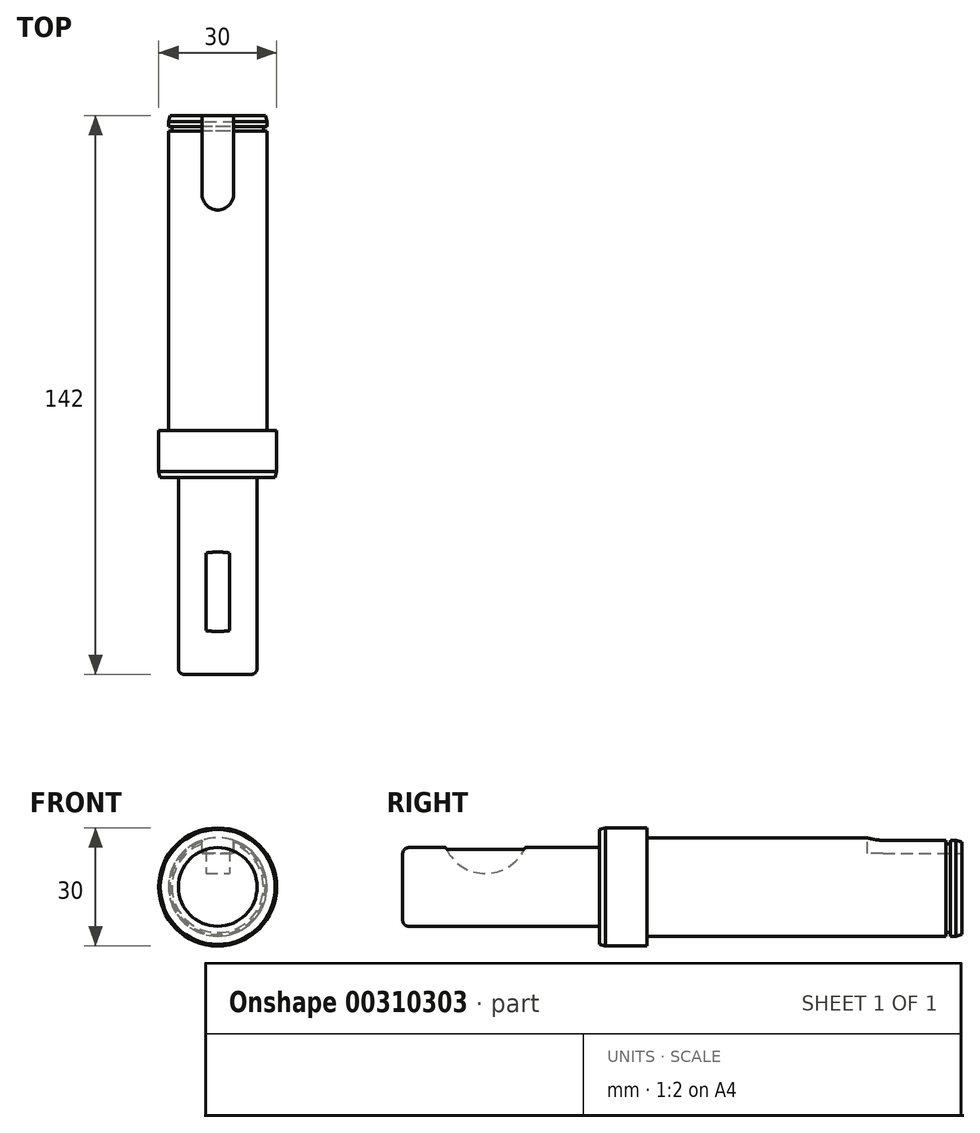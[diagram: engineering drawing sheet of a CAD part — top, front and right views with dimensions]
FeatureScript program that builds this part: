
annotation { "Feature Type Name" : "Feature", "Feature Type Description" : "" }
export const myFeature = defineFeature(function(context is Context, id is Id, definition is map)
    precondition{}
    {
        {
            var Q0;
            Q0=qCreatedBy(makeId("Front.planeOp"),FACE);
            var sketch = newSketch(context, id + "F0", { "sketchPlane" : qUnion([Q0])});
            skCircle(sketch, "E0", {"center": v(0, 0) * mm, "radius": 12.5 * mm});
            skSolve(sketch);
        }
        {
            var Q0;
            Q0=makeQuery(id+"F0.imprint","IMPRINT",FACE,{"disambiguationData":[TD([[makeQuery(id+"F0.imprint","IMPRINT",EDGE,{"derivedFrom":sQuery(id+"F0.wireOp",EDGE,"E0")}),1.0]])]});
            extrude(context, id + "F1", {"entities" : qUnion([Q0]), "depth" : 80 * mm});
        }
        {
            var Q0;
            Q0=makeQuery(id+"F1.opExtrude","CAP_FACE",FACE,{"disambiguationData":[OSD([sQuery(id+"F0.wireOp",EDGE,"E0")])],"isStart":false});
            var sketch = newSketch(context, id + "F2", { "sketchPlane" : qUnion([Q0])});
            skCircle(sketch, "E1", {"center": v(0, 0) * mm, "radius": 15 * mm});
            skSolve(sketch);
        }
        {
            var Q0;
            Q0 = qSketchRegion(id + "F2", true);
            var Q1;
            Q1=sQuery(id+"F2.wireOp",EDGE,"E1");
            extrude(context, id + "F3", {"entities" : qUnion([Q0]), "operationType" : NewBodyOperationType.ADD, "surfaceEntities" : qUnion([Q1]), "depth" : 12 * mm});
        }
        {
            var Q0;
            Q0=makeQuery(id+"F3.opExtrude","CAP_FACE",FACE,{"disambiguationData":[OSD([sQuery(id+"F2.wireOp",EDGE,"E1")])],"isStart":false});
            var sketch = newSketch(context, id + "F4", { "sketchPlane" : qUnion([Q0])});
            skCircle(sketch, "E2", {"center": v(0, 0) * mm, "radius": 10 * mm});
            skSolve(sketch);
        }
        {
            var Q0;
            Q0=makeQuery(id+"F4.imprint","IMPRINT",FACE,{"disambiguationData":[TD([[makeQuery(id+"F4.imprint","IMPRINT",EDGE,{"derivedFrom":sQuery(id+"F4.wireOp",EDGE,"E2")}),1.0]])]});
            extrude(context, id + "F5", {"entities" : qUnion([Q0]), "operationType" : NewBodyOperationType.ADD, "depth" : 50 * mm});
        }
        {
            var Q0;
            Q0=makeQuery(id+"F1.opExtrude","CAP_EDGE",EDGE,{"disambiguationData":[OSD([sQuery(id+"F0.wireOp",EDGE,"E0")])],"isStart":true});
            chamfer(context, id + "F6", {"entities" : qUnion([Q0]), "chamferType" : ChamferType.OFFSET_ANGLE, "width" : 0.4 * mm, "oppositeDirection" : true, "angle" : 75 * degree, "tangentPropagation" : true});
        }
        {
            var Q0;
            Q0=makeQuery(id+"F3.opExtrude","CAP_EDGE",EDGE,{"disambiguationData":[OSD([sQuery(id+"F2.wireOp",EDGE,"E1")])],"isStart":false});
            chamfer(context, id + "F7", {"entities" : qUnion([Q0]), "chamferType" : ChamferType.OFFSET_ANGLE, "width" : 0.4 * mm, "oppositeDirection" : false, "angle" : 75 * degree, "tangentPropagation" : true});
        }
        {
            var Q0;
            Q0=makeQuery(id+"F5.opExtrude","CAP_EDGE",EDGE,{"disambiguationData":[OSD([sQuery(id+"F4.wireOp",EDGE,"E2")])],"isStart":false});
            fillet(context, id + "F8", {"entities" : qUnion([Q0]), "radius" : 1.5 * mm, "tangentPropagation" : true, "allowEdgeOverflow" : false});
        }
        {
            var Q0;
            Q0=qCreatedBy(makeId("Top.planeOp"),FACE);
            cPlane(context, id + "F9", {"entities" : qUnion([Q0]), "cplaneType" : CPlaneType.OFFSET, "offset" : 12.5 * mm, "width" : 150 * mm, "height" : 150 * mm});
        }
        {
            var Q0;
            Q0=qCreatedBy(id+"F9.planeOp",FACE);
            var sketch = newSketch(context, id + "F10", { "sketchPlane" : qUnion([Q0])});
            skLineSegment(sketch, "E3", {"start": v(-4, -20) * mm, "end": v(-4, 31.78) * mm});
            skLineSegment(sketch, "E4", {"start": v(-4, 31.78) * mm, "end": v(4, 31.78) * mm});
            skLineSegment(sketch, "E5", {"start": v(4, 31.78) * mm, "end": v(4, -20) * mm});
            skArc(sketch, "E6", {"start": v(-4, -20) * mm, "mid": v(0, -24) * mm, "end": v(4, -20) * mm});
            skSolve(sketch);
        }
        {
            var Q0;
            Q0=makeQuery(id+"F10.imprint","IMPRINT",FACE,{"disambiguationData":[TD([[makeQuery(id+"F10.imprint","IMPRINT",EDGE,{"derivedFrom":sQuery(id+"F10.wireOp",EDGE,"E3")}),-1.0]])]});
            extrude(context, id + "F11", {"entities" : qUnion([Q0]), "operationType" : NewBodyOperationType.REMOVE, "oppositeDirection" : true, "depth" : 4 * mm});
        }
        {
            var Q0;
            Q0=qCreatedBy(makeId("Right.planeOp"),FACE);
            var sketch = newSketch(context, id + "F12", { "sketchPlane" : qUnion([Q0])});
            skLineSegment(sketch, "E7", {"start": v(-2.8, -11.6) * mm, "end": v(-2.8, -12.5) * mm});
            skLineSegment(sketch, "E8", {"start": v(-2.8, -12.5) * mm, "end": v(-4, -12.5) * mm});
            skLineSegment(sketch, "E9", {"start": v(-4, -12.5) * mm, "end": v(-4, -11.6) * mm});
            skLineSegment(sketch, "E10", {"start": v(-4, -11.6) * mm, "end": v(-2.8, -11.6) * mm});
            skSolve(sketch);
        }
        {
            var Q0;
            Q0 = qSketchRegion(id + "F12", true);
            var Q1;
            Q1=makeQuery(id+"F1.opExtrude","SWEPT_FACE",FACE,{"disambiguationData":[OSD([sQuery(id+"F0.wireOp",EDGE,"E0")])]});
            revolve(context, id + "F13", {"operationType" : NewBodyOperationType.REMOVE, "entities" : qUnion([Q0]), "axis" : qUnion([Q1]), "revolveType" : RevolveType.FULL, "oppositeDirection" : true});
        }
        {
            var Q0;
            Q0=qCreatedBy(makeId("Right.planeOp"),FACE);
            var sketch = newSketch(context, id + "F14", { "sketchPlane" : qUnion([Q0])});
            skCircle(sketch, "E11", {"center": v(-121, 14.4) * mm, "radius": 11 * mm});
            skSolve(sketch);
        }
        {
            var Q0;
            Q0=makeQuery(id+"F14.imprint","IMPRINT",FACE,{"disambiguationData":[TD([[makeQuery(id+"F14.imprint","IMPRINT",EDGE,{"derivedFrom":sQuery(id+"F14.wireOp",EDGE,"E11")}),1.0]])]});
            var Q1;
            Q1=sQuery(id+"F14.wireOp",EDGE,"E11");
            extrude(context, id + "F15", {"entities" : qUnion([Q0]), "operationType" : NewBodyOperationType.REMOVE, "surfaceEntities" : qUnion([Q1]), "endBound" : BoundingType.SYMMETRIC, "oppositeDirection" : true, "depth" : 6 * mm});
        }
    });
